# Revit family: Control_Unit-Lutron-HomeWorks_Panel_Interface-HQ-MI-LX NEW
name_source: partatom
category: Lighting Devices
units: mm (PartAtom-declared; Revit-internal decimal feet)

## family parameters
Always vertical = No
Cut with Voids When Loaded = No
Maintain Annotation Orientation = No
OmniClass Number = 23.80.30.11.17
OmniClass Title = Distribution Boards and Control Panels
Part Type = Normal
Room Calculation Point = No
Round Connector Dimension = Use Diameter
Shared = No
Work Plane-Based = Yes

## types (1)
- HQ-MI-LX
    Apparent Load = 0 VA
    Assembly Code = D5020200
    Cost = 0 $
    Default Elevation = 0 "
    Description = The panel link to QS link translator provides an interface
for legacy remote power modules and
specification-grade panels.
    Finish = Metal - Lutron - White - Matte
    Frequency = 60 Hz
    Instruction Sheet Link = Contact Manufacturer for Installation Information
    Keynote = 26 51 00
    Load Classification = Lighting
    Manufacturer = Lutron Electronics Co., Inc
    Manufacturer Fax Number = 610-282-1243
    Maximum Operating Temperature = 104 °F
    Minimum Operating Temperature = 32 °F
    Model = HQ-MI-LX
    Number of Poles = 1
    Operating Voltage = 24 V~ 50/60 Hz or 24-36 V- 250 mA
    Overall Depth = 1.9 "
    Overall Height = 10.75 "
    Overall Width = 3.43 "
    Performance URL = Contact Manufacturer for Performance Information
    Power Factor = 1
    Product Documentation Link = https://assets.lutron.com
    Product Name = HomeWorks Panel Link Translator
    Product Page URL = https://residential.lutron.com
    Series = HomeWorks
    URL = https://www.lutron.com
    Version = 2020 - v1.0a
    Video Link = https://www.youtube.com
    Voltage = 24 V
    Voltage Comment = 24 V~ 50/60 Hz or 24-36 V- 250 mA
    Warranty URL = https://www.lutron.com

## geometry (parser evidence)
native form markers: Sweep x2
no freeform markers — native parametric forms only
